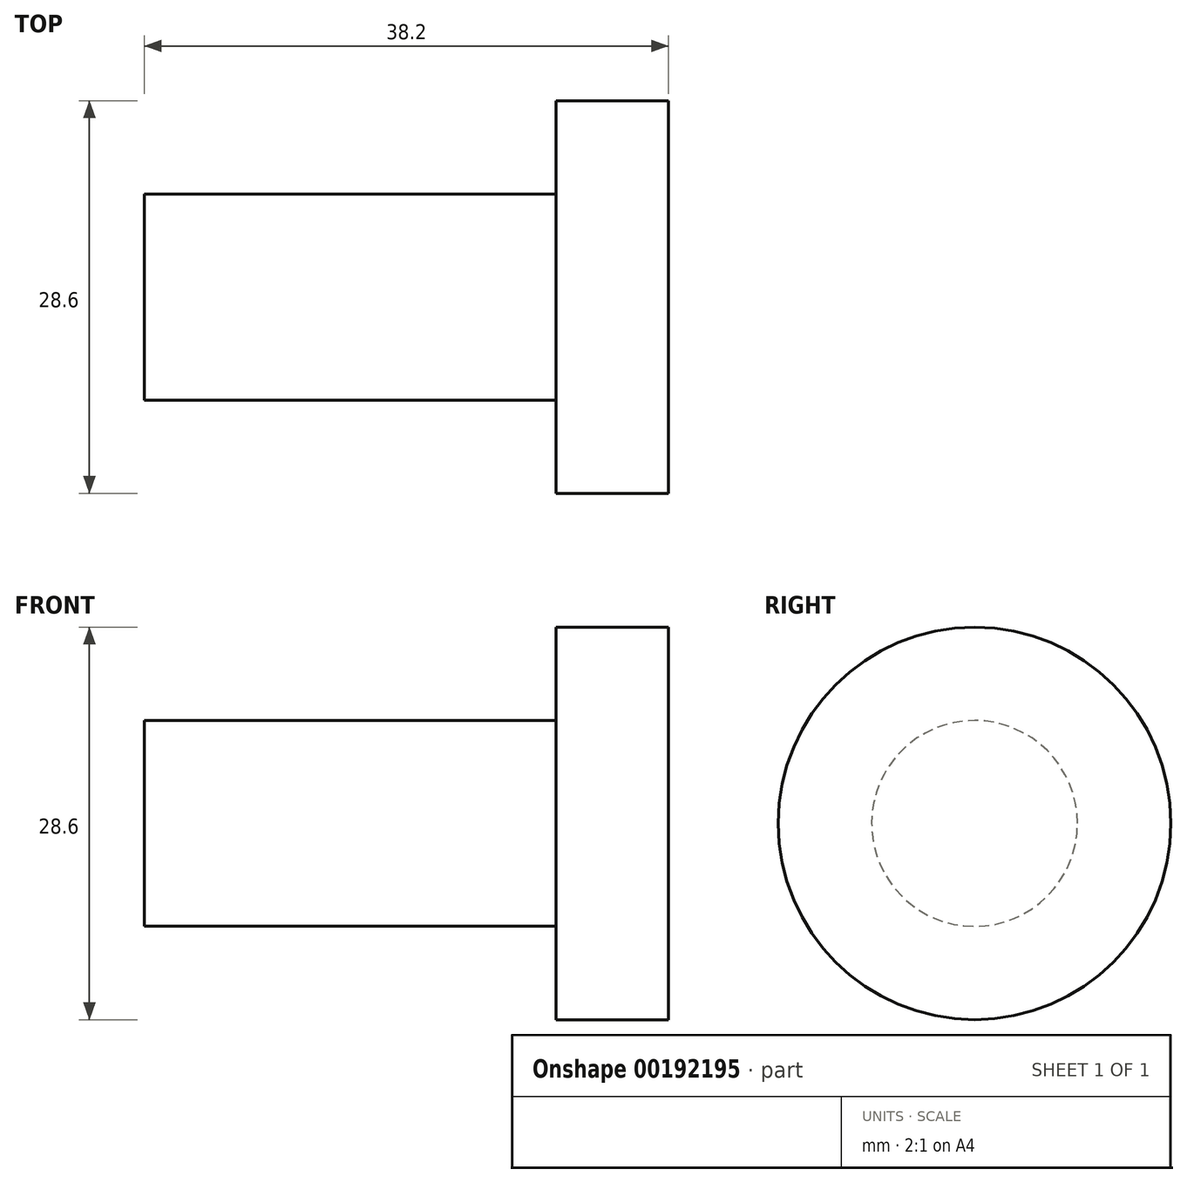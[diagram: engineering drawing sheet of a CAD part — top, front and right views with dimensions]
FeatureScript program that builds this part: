
annotation { "Feature Type Name" : "Feature", "Feature Type Description" : "" }
export const myFeature = defineFeature(function(context is Context, id is Id, definition is map)
    precondition{}
    {
        {
            var Q0;
            Q0=qCreatedBy(makeId("Front.planeOp"),FACE);
            var sketch = newSketch(context, id + "F0", { "sketchPlane" : qUnion([Q0])});
            skLineSegment(sketch, "E0.bottom", {"start": v(15, -7.5) * mm, "end": v(-15, -7.5) * mm});
            skLineSegment(sketch, "E0.top", {"start": v(15, 7.5) * mm, "end": v(-15, 7.5) * mm});
            skLineSegment(sketch, "E0.left", {"start": v(15, -7.5) * mm, "end": v(15, 7.5) * mm});
            skLineSegment(sketch, "E0.right", {"start": v(-15, -7.5) * mm, "end": v(-15, 7.5) * mm});
            skPoint(sketch, "E0.middle", {"position": v(0, 0) * mm});
            skLineSegment(sketch, "E1", {"start": v(-15, 0) * mm, "end": v(15, 0) * mm});
            skSolve(sketch);
        }
        {
            var Q0;
            {var subQ0=sQuery(id+"F0.wireOp",EDGE,"E0.top");Q0=makeQuery(id+"F0.imprint","IMPRINT",FACE,{"disambiguationData":[TD([[makeQuery(id+"F0.imprint","IMPRINT",EDGE,{"derivedFrom":subQ0}),1.0]])]});}
            var Q1;
            Q1=sQuery(id+"F0.wireOp",EDGE,"E1");
            revolve(context, id + "F1", {"entities" : qUnion([Q0]), "axis" : qUnion([Q1]), "revolveType" : RevolveType.FULL});
        }
        {
            var Q0;
            Q0=makeQuery(id+"F1.opRevolve","SWEPT_FACE",FACE,{"disambiguationData":[OSD([sQuery(id+"F0.wireOp",EDGE,"E0.left")])]});
            var sketch = newSketch(context, id + "F2", { "sketchPlane" : qUnion([Q0])});
            skCircle(sketch, "E2", {"center": v(0, 0) * mm, "radius": 14.3 * mm});
            skSolve(sketch);
        }
        {
            var Q0;
            Q0=makeQuery(id+"F2.imprint","IMPRINT",FACE,{"disambiguationData":[TD([[makeQuery(id+"F2.imprint","IMPRINT",EDGE,{"derivedFrom":sQuery(id+"F2.wireOp",EDGE,"E2")}),1.0]])]});
            var Q1;
            Q1=makeQuery(id+"F2.imprint","IMPRINT",FACE,{"disambiguationData":[TD([[makeQuery(id+"F2.imprint","IMPRINT",EDGE,{"derivedFrom":makeQuery(id+"F1.opRevolve","SWEPT_EDGE",EDGE,{"disambiguationData":[OSD([sQuery(id+"F0.wireOp",EDGE,"E0.top"),sQuery(id+"F0.wireOp",EDGE,"E0.left")])]})}),-1.0]])]});
            extrude(context, id + "F3", {"entities" : qUnion([Q0, Q1]), "operationType" : NewBodyOperationType.ADD, "depth" : 8.2 * mm});
        }
    });
